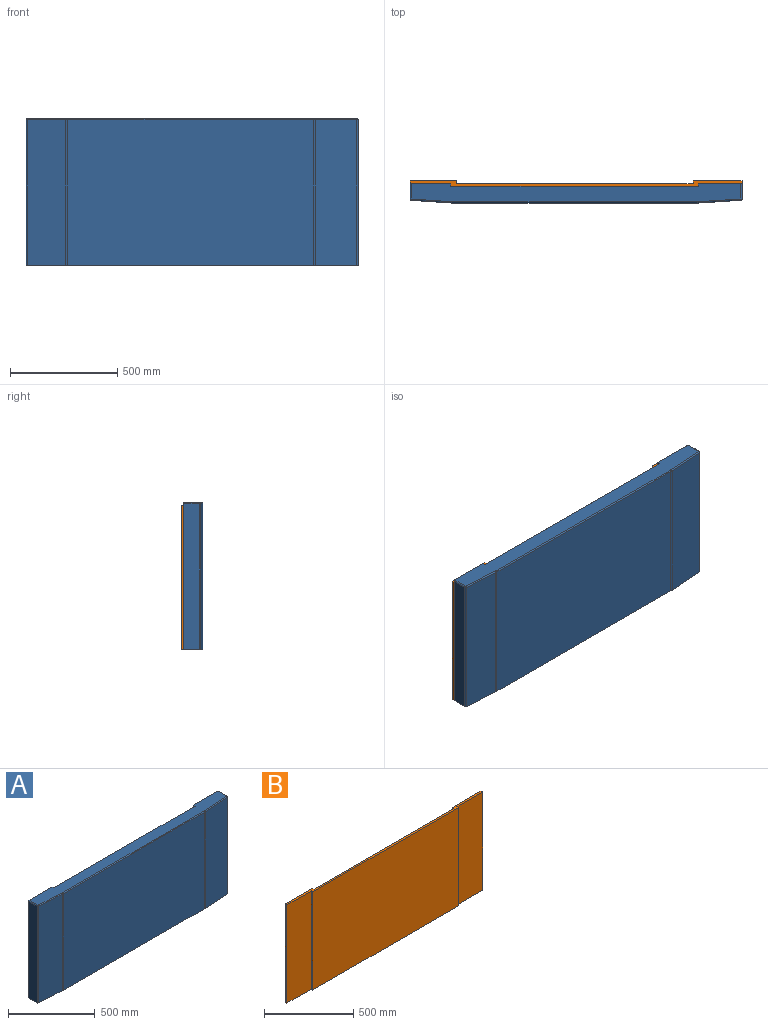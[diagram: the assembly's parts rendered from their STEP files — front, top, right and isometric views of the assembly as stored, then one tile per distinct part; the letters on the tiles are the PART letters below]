
ASSEMBLY  parts=2 mates=1
PART A: 25 faces, bbox 1549.4x89x685.8 mm
  f0: plane 1539.24x83.82mm, normal (0,0,1), area 111964.7mm2, adj f5,f6,f7,f8,f9,f13,f15,f16
  f1: plane 680.72x181.54mm, normal (-0.07,-1,0), area 123851.3mm2, adj f11,f12,f15,f23
  f2: plane 1147.51x680.72mm, normal (0,-1,0), area 781130.6mm2, adj f11,f16,f21,f23
  f3: plane 680.72x194.48mm, normal (0.06,-1,0), area 132644.6mm2, adj f11,f17,f20,f21
  f4: plane 680.72x71.43mm, normal (1,0,0), area 48622.2mm2, adj f5,f11,f18,f20
  f5: plane 685.8x203.2mm, normal (0,1,0), area 139349mm2, adj f0,f4,f6,f11,f18
  f6: plane 685.8x12.7mm, normal (-1,0,0), area 8709.7mm2, adj f0,f5,f7,f11
  f7: plane 1155.7x685.8mm, normal (0,1,0), area 792579.1mm2, adj f0,f6,f8,f11
  f8: plane 685.8x12.7mm, normal (1,0,0), area 8709.7mm2, adj f0,f7,f9,f11
  f9: plane 685.8x190.5mm, normal (0,1,0), area 130639.4mm2, adj f0,f8,f10,f11,f13
  f10: plane 680.72x71.45mm, normal (-1,0,0), area 48635.7mm2, adj f9,f11,f12,f13
  f11: plane 1549.4x88.9mm, normal (0,0,-1), area 120554.4mm2, adj f1,f2,f3,f4,f5,f6,f7,f8
  f12: cylinder r=5.08mm len=680.72mm, axis (0,0,1), area 5201.7mm2, adj f1,f10,f11,f14
  f13: cylinder r=5.08mm len=71.45mm, axis (0,1,0), area 570.1mm2, adj f0,f9,f10,f14
  f14: sphere r=5.08mm, area 38.8mm2, adj f12,f13,f15
  f15: cylinder r=5.08mm len=181.88mm, axis (-1,0.07,0), area 1451.8mm2, adj f0,f1,f14,f24
  f16: cylinder r=5.08mm len=1147.51mm, axis (-1,0,0), area 9156.7mm2, adj f0,f2,f22,f24
  f17: cylinder r=5.08mm len=194.8mm, axis (-1,-0.06,0), area 1554.9mm2, adj f0,f3,f19,f22
  f18: cylinder r=5.08mm len=71.43mm, axis (0,-1,0), area 570mm2, adj f0,f4,f5,f19
  f19: sphere r=5.08mm, area 38.9mm2, adj f17,f18,f20
  f20: cylinder r=5.08mm len=680.72mm, axis (0,0,-1), area 5216.1mm2, adj f3,f4,f11,f19
  f21: cylinder r=127mm len=680.72mm, axis (0,0,-1), area 5396.2mm2, adj f2,f3,f11,f22
  f22: torus R=121.92mm, axis (0,0,1), area 62.3mm2, adj f0,f16,f17,f21
  f23: cylinder r=127mm len=680.72mm, axis (0,0,-1), area 5754.9mm2, adj f1,f2,f11,f24
  f24: torus R=121.92mm, axis (0,0,1), area 66.5mm2, adj f0,f15,f16,f23
PART B: 14 faces, bbox 1549.4x25.4x673.1 mm
  f0: plane 673.1x190.5mm, normal (0,-1,0), area 128225.6mm2, adj f1,f11,f12,f13
  f1: plane 673.1x12.7mm, normal (-1,0,0), area 8548.4mm2, adj f0,f2,f12,f13
  f2: plane 1155.7x673.1mm, normal (0,-1,0), area 777901.7mm2, adj f1,f3,f12,f13
  f3: plane 673.1x12.7mm, normal (1,0,0), area 8548.4mm2, adj f2,f4,f12,f13
  f4: plane 673.1x203.2mm, normal (0,-1,0), area 136773.9mm2, adj f3,f5,f12,f13
  f5: plane 673.1x12.7mm, normal (1,0,0), area 8548.4mm2, adj f4,f6,f12,f13
  f6: plane 673.1x228.6mm, normal (0,1,0), area 153870.7mm2, adj f5,f7,f12,f13
  f7: plane 673.1x12.7mm, normal (-1,0,0), area 8548.4mm2, adj f6,f8,f12,f13
  f8: plane 1104.9x673.1mm, normal (0,1,0), area 743708.2mm2, adj f7,f9,f12,f13
  f9: plane 673.1x12.7mm, normal (1,0,0), area 8548.4mm2, adj f8,f10,f12,f13
  f10: plane 673.1x215.9mm, normal (0,1,0), area 145322.3mm2, adj f9,f11,f12,f13
  f11: plane 673.1x12.7mm, normal (-1,0,0), area 8548.4mm2, adj f0,f10,f12,f13
  f12: plane 1549.4x25.4mm, normal (0,0,1), area 20322.5mm2, adj f0,f1,f2,f3,f4,f5,f6,f7
  f13: plane 1549.4x25.4mm, normal (0,0,-1), area 20322.5mm2, adj f0,f1,f2,f3,f4,f5,f6,f7
PLACE A t=(-1052.06,174.69,567.83)mm
PLACE B t=(-1052.06,174.69,567.83)mm
MATE fastened B.f2 <-> A.f7  axis (0,-1,0) through (-1629.91,174.69,567.83)mm
